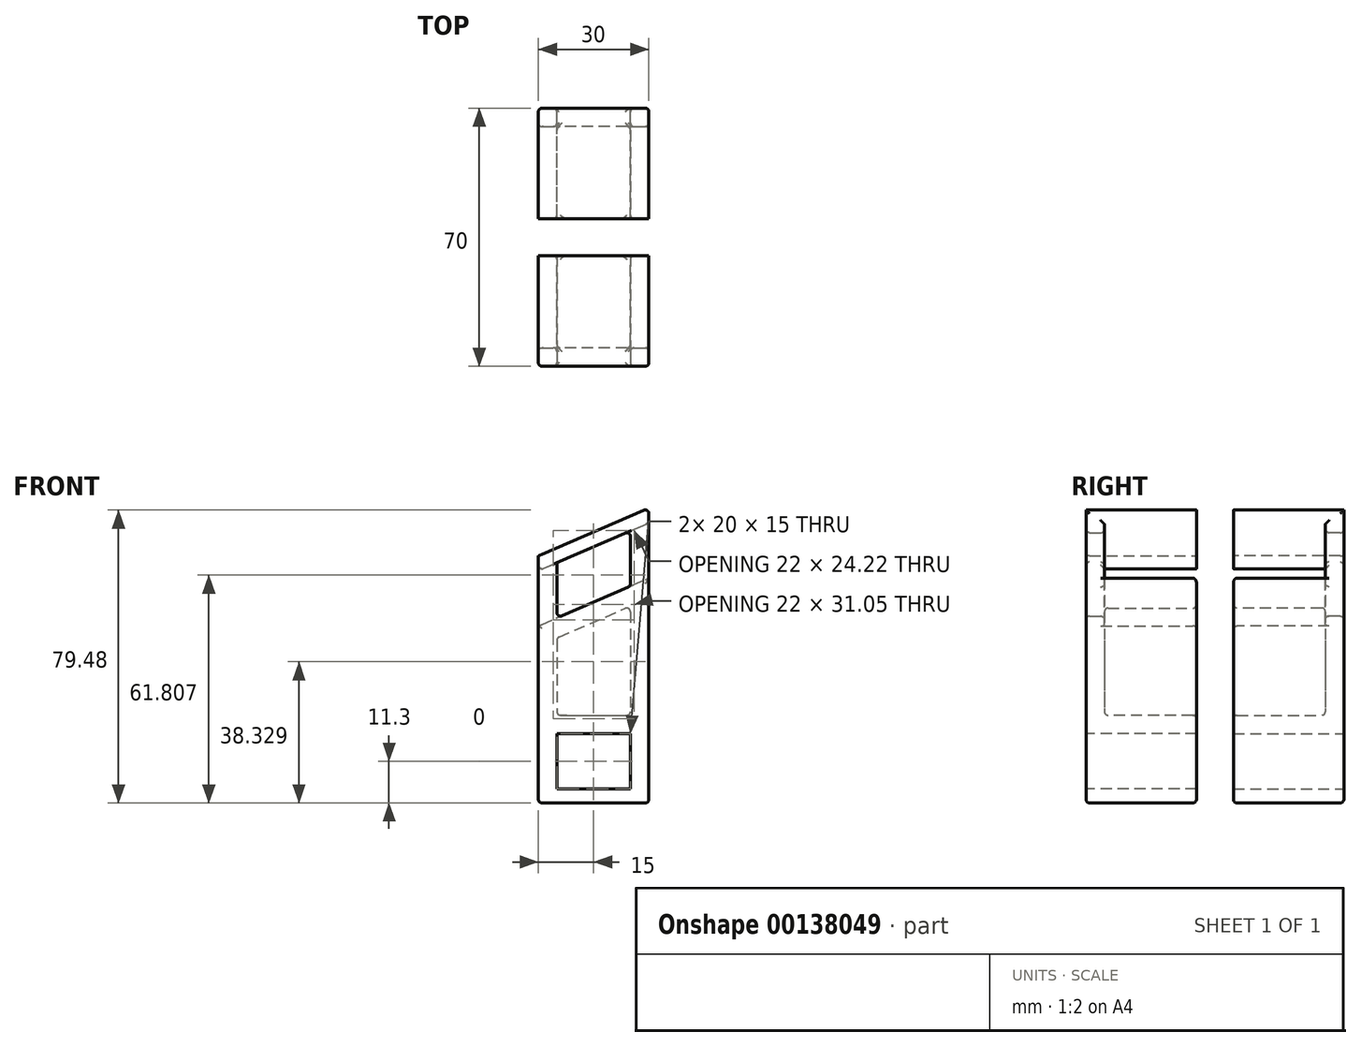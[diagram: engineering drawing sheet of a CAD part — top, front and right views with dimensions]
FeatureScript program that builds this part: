
annotation { "Feature Type Name" : "Feature", "Feature Type Description" : "" }
export const myFeature = defineFeature(function(context is Context, id is Id, definition is map)
    precondition{}
    {
        {
            var Q0;
            Q0=qCreatedBy(makeId("Top.planeOp"),FACE);
            var sketch = newSketch(context, id + "F0", { "sketchPlane" : qUnion([Q0])});
            skLineSegment(sketch, "E0.bottom", {"start": v(-15, 15) * mm, "end": v(15, 15) * mm});
            skLineSegment(sketch, "E0.top", {"start": v(-15, -15) * mm, "end": v(15, -15) * mm});
            skLineSegment(sketch, "E0.left", {"start": v(-15, 15) * mm, "end": v(-15, -15) * mm});
            skLineSegment(sketch, "E0.right", {"start": v(15, 15) * mm, "end": v(15, -15) * mm});
            skSolve(sketch);
        }
        {
            var Q0;
            Q0 = qSketchRegion(id + "F0", true);
            extrude(context, id + "F1", {"entities" : qUnion([Q0]), "depth" : 80 * mm});
        }
        {
            var Q0;
            Q0=qCreatedBy(makeId("Top.planeOp"),FACE);
            cPlane(context, id + "F2", {"entities" : qUnion([Q0]), "cplaneType" : CPlaneType.OFFSET, "offset" : 76 * mm, "width" : 152.4 * mm, "height" : 152.4 * mm});
        }
        {
            var Q0;
            Q0=qCreatedBy(id+"F2.planeOp",FACE);
            var sketch = newSketch(context, id + "F3", { "sketchPlane" : qUnion([Q0])});
            skLineSegment(sketch, "E1", {"start": v(15.02, 15.02) * mm, "end": v(15.02, -15.02) * mm});
            skSolve(sketch);
        }
        {
            var Q0;
            Q0=makeQuery(id+"F1.opExtrude","SWEPT_FACE",FACE,{"disambiguationData":[OSD([sQuery(id+"F0.wireOp",EDGE,"E0.right")])]});
            var sketch = newSketch(context, id + "F4", { "sketchPlane" : qUnion([Q0])});
            skLineSegment(sketch, "E2.bottom", {"start": v(-15, 76) * mm, "end": v(15, 76) * mm});
            skLineSegment(sketch, "E2.top", {"start": v(-15, 61) * mm, "end": v(15, 61) * mm});
            skLineSegment(sketch, "E2.left", {"start": v(-15, 76) * mm, "end": v(-15, 61) * mm});
            skLineSegment(sketch, "E2.right", {"start": v(15, 76) * mm, "end": v(15, 61) * mm});
            skSolve(sketch);
        }
        {
            var Q0;
            Q0=makeQuery(id+"F1.opExtrude","SWEPT_FACE",FACE,{"disambiguationData":[OSD([sQuery(id+"F0.wireOp",EDGE,"E0.left")])]});
            var sketch = newSketch(context, id + "F5", { "sketchPlane" : qUnion([Q0])});
            skLineSegment(sketch, "E3.bottom", {"start": v(-15, 63) * mm, "end": v(15, 63) * mm});
            skLineSegment(sketch, "E3.top", {"start": v(-15, 48) * mm, "end": v(15, 48) * mm});
            skLineSegment(sketch, "E3.left", {"start": v(-15, 63) * mm, "end": v(-15, 48) * mm});
            skLineSegment(sketch, "E3.right", {"start": v(15, 63) * mm, "end": v(15, 48) * mm});
            skSolve(sketch);
        }
        {
            var Q1;
            Q1=makeQuery(id+"F5.imprint","IMPRINT",FACE,{"disambiguationData":[TD([[makeQuery(id+"F5.imprint","IMPRINT",EDGE,{"derivedFrom":sQuery(id+"F5.wireOp",EDGE,"E3.bottom")}),-1.0]])]});
            var Q2;
            Q2=makeQuery(id+"F4.imprint","IMPRINT",FACE,{"disambiguationData":[TD([[makeQuery(id+"F4.imprint","IMPRINT",EDGE,{"derivedFrom":sQuery(id+"F4.wireOp",EDGE,"E2.bottom")}),-1.0]])]});
            loft(context, id + "F6", {"operationType" : NewBodyOperationType.REMOVE, "sheetProfilesArray" : [{ "sheetProfileEntities" : qUnion([Q1]) }, { "sheetProfileEntities" : qUnion([Q2]) }]});
        }
        {
            var Q0;
            Q0=makeQuery(id+"F1.opExtrude","CAP_FACE",FACE,{"disambiguationData":[OSD([sQuery(id+"F0.wireOp",EDGE,"E0.bottom"),sQuery(id+"F0.wireOp",EDGE,"E0.top"),sQuery(id+"F0.wireOp",EDGE,"E0.left"),sQuery(id+"F0.wireOp",EDGE,"E0.right")])],"isStart":false});
            var sketch = newSketch(context, id + "F7", { "sketchPlane" : qUnion([Q0])});
            skLineSegment(sketch, "E4.bottom", {"start": v(15, 15) * mm, "end": v(-15, 15) * mm});
            skLineSegment(sketch, "E4.top", {"start": v(15, 10) * mm, "end": v(-15, 10) * mm});
            skLineSegment(sketch, "E4.left", {"start": v(15, 15) * mm, "end": v(15, 10) * mm});
            skLineSegment(sketch, "E4.right", {"start": v(-15, 15) * mm, "end": v(-15, 10) * mm});
            skSolve(sketch);
        }
        {
            var Q0;
            Q0=makeQuery(id+"F7.imprint","IMPRINT",FACE,{"disambiguationData":[TD([[makeQuery(id+"F7.imprint","IMPRINT",EDGE,{"derivedFrom":sQuery(id+"F7.wireOp",EDGE,"E4.bottom")}),-1.0]])]});
            var Q1;
            Q1=makeQuery(id+"F6.boolean.opBoolean","SPLIT",BODY,{"disambiguationData":[OD(0.0)],"derivedFrom":makeQuery(id+"F1.opExtrude","SWEPT_BODY",BODY,{"disambiguationData":[OSD([sQuery(id+"F0.wireOp",EDGE,"E0.bottom"),sQuery(id+"F0.wireOp",EDGE,"E0.top"),sQuery(id+"F0.wireOp",EDGE,"E0.left"),sQuery(id+"F0.wireOp",EDGE,"E0.right")])]})});
            extrude(context, id + "F8", {"entities" : qUnion([Q0]), "oppositeDirection" : true, "endBoundEntityBody" : qUnion([Q1]), "depth" : 76.2 * mm});
        }
        {
            var Q0;
            Q0=makeQuery(id+"F8.opExtrude","SWEPT_FACE",FACE,{"disambiguationData":[OSD([sQuery(id+"F7.wireOp",EDGE,"E4.bottom")])]});
            var sketch = newSketch(context, id + "F9", { "sketchPlane" : qUnion([Q0])});
            skLineSegment(sketch, "E5", {"start": v(-15, 3.8) * mm, "end": v(-15, 18.8) * mm});
            skLineSegment(sketch, "E6", {"start": v(15, 3.8) * mm, "end": v(15, 18.8) * mm});
            skLineSegment(sketch, "E7", {"start": v(15, 18.8) * mm, "end": v(-15, 18.8) * mm});
            skLineSegment(sketch, "E8", {"start": v(15, 3.8) * mm, "end": v(-15, 3.8) * mm});
            skSolve(sketch);
        }
        {
            var Q0;
            Q0=makeQuery(id+"F9.imprint","IMPRINT",FACE,{"disambiguationData":[TD([[makeQuery(id+"F9.imprint","IMPRINT",EDGE,{"derivedFrom":sQuery(id+"F9.wireOp",EDGE,"E5")}),-1.0]])]});
            var sketch = newSketch(context, id + "F10", { "sketchPlane" : qUnion([Q0])});
            skLineSegment(sketch, "E9.0", {"start": v(-10, 3.8) * mm, "end": v(-10, 18.8) * mm});
            skLineSegment(sketch, "E10.0", {"start": v(10, 3.8) * mm, "end": v(10, 18.8) * mm});
            skLineSegment(sketch, "E11", {"start": v(-10, 18.8) * mm, "end": v(10, 18.8) * mm});
            skLineSegment(sketch, "E12", {"start": v(-10, 3.8) * mm, "end": v(10, 3.8) * mm});
            skSolve(sketch);
        }
        {
            var Q0;
            Q0=makeQuery(id+"F10.imprint","IMPRINT",FACE,{"disambiguationData":[TD([[makeQuery(id+"F10.imprint","IMPRINT",EDGE,{"derivedFrom":sQuery(id+"F10.wireOp",EDGE,"E9.0")}),-1.0]])]});
            extrude(context, id + "F11", {"entities" : qUnion([Q0]), "operationType" : NewBodyOperationType.REMOVE, "endBound" : BoundingType.THROUGH_ALL, "oppositeDirection" : true, "depth" : 25.4 * mm});
        }
        {
            var Q0;
            {var subQ0=sQuery(id+"F0.wireOp",EDGE,"E0.right");var subQ1=sQuery(id+"F0.wireOp",EDGE,"E0.left");var subQ2=sQuery(id+"F0.wireOp",EDGE,"E0.top");var subQ3=sQuery(id+"F0.wireOp",EDGE,"E0.bottom");Q0=makeQuery(id+"F6.boolean.opBoolean","SPLIT",FACE,{"disambiguationData":[TD([makeQuery(id+"F1.opExtrude","CAP_FACE",FACE,{"disambiguationData":[OSD([subQ3,subQ2,subQ1,subQ0])],"isStart":true})])],"derivedFrom":makeQuery(id+"F1.opExtrude","SWEPT_FACE",FACE,{"disambiguationData":[OSD([subQ2])]})});}
            shell(context, id + "F12", {"entities" : qUnion([Q0]), "thickness" : 5 * mm});
        }
        {
            var Q0;
            {var subQ0=sQuery(id+"F9.wireOp",EDGE,"E7");Q0=makeQuery(id+"F9.imprint","IMPRINT",FACE,{"disambiguationData":[TD([[makeQuery(id+"F9.imprint","IMPRINT",EDGE,{"derivedFrom":subQ0}),-1.0]])]});}
            var sketch = newSketch(context, id + "F13", { "sketchPlane" : qUnion([Q0])});
            skLineSegment(sketch, "E13", {"start": v(-10, 73.83) * mm, "end": v(10, 65.17) * mm});
            skLineSegment(sketch, "E14", {"start": v(10, 65.17) * mm, "end": v(10, 50.17) * mm});
            skLineSegment(sketch, "E15", {"start": v(10, 50.17) * mm, "end": v(-10, 58.83) * mm});
            skLineSegment(sketch, "E16", {"start": v(-10, 58.83) * mm, "end": v(-10, 73.83) * mm});
            skSolve(sketch);
        }
        {
            var Q0;
            Q0=makeQuery(id+"F13.imprint","IMPRINT",FACE,{"disambiguationData":[TD([[makeQuery(id+"F13.imprint","IMPRINT",EDGE,{"derivedFrom":sQuery(id+"F13.wireOp",EDGE,"E13")}),-1.0]])]});
            extrude(context, id + "F14", {"entities" : qUnion([Q0]), "operationType" : NewBodyOperationType.REMOVE, "oppositeDirection" : true, "depth" : 25.4 * mm});
        }
        {
            var Q0;
            Q0=makeQuery(id+"F14.boolean.opBoolean","COPY",FACE,{"derivedFrom":makeQuery(id+"F14.opExtrude","SWEPT_FACE",FACE,{"disambiguationData":[OSD([sQuery(id+"F13.wireOp",EDGE,"E16")])]})});
            var Q1;
            Q1=makeQuery(id+"F14.boolean.opBoolean","COPY",FACE,{"derivedFrom":makeQuery(id+"F14.opExtrude","SWEPT_FACE",FACE,{"disambiguationData":[OSD([sQuery(id+"F13.wireOp",EDGE,"E15")])]})});
            var Q2;
            Q2=makeQuery(id+"F14.boolean.opBoolean","COPY",FACE,{"derivedFrom":makeQuery(id+"F14.opExtrude","SWEPT_FACE",FACE,{"disambiguationData":[OSD([sQuery(id+"F13.wireOp",EDGE,"E14")])]})});
            var Q3;
            Q3=makeQuery(id+"F14.boolean.opBoolean","COPY",EDGE,{"derivedFrom":makeQuery(id+"F14.opExtrude","CAP_EDGE",EDGE,{"disambiguationData":[OSD([sQuery(id+"F13.wireOp",EDGE,"E13")])],"isStart":true})});
            fillet(context, id + "F15", {"entities" : qUnion([Q0, Q1, Q2, Q3]), "radius" : 1 * mm, "tangentPropagation" : true, "allowEdgeOverflow" : false});
        }
        {
            var Q0;
            Q0=makeQuery(id+"F12.opShell","OFFSET_FACE",FACE,{"disambiguationData":[OSD([sQuery(id+"F0.wireOp",EDGE,"E0.right")])]});
            var Q1;
            Q1=makeQuery(id+"F12.opShell","OFFSET_FACE",FACE,{"disambiguationData":[OSD([sQuery(id+"F0.wireOp",EDGE,"E0.bottom"),sQuery(id+"F0.wireOp",EDGE,"E0.top"),sQuery(id+"F0.wireOp",EDGE,"E0.left"),sQuery(id+"F0.wireOp",EDGE,"E0.right"),sQuery(id+"F4.wireOp",EDGE,"E2.top"),sQuery(id+"F4.wireOp",EDGE,"E2.left"),sQuery(id+"F4.wireOp",EDGE,"E2.right"),sQuery(id+"F5.wireOp",EDGE,"E3.top"),sQuery(id+"F5.wireOp",EDGE,"E3.left"),sQuery(id+"F5.wireOp",EDGE,"E3.right")])]});
            var Q2;
            Q2=makeQuery(id+"F12.opShell","OFFSET_FACE",FACE,{"disambiguationData":[OSD([sQuery(id+"F0.wireOp",EDGE,"E0.bottom"),sQuery(id+"F0.wireOp",EDGE,"E0.top"),sQuery(id+"F0.wireOp",EDGE,"E0.left"),sQuery(id+"F0.wireOp",EDGE,"E0.right")])]});
            var Q3;
            Q3=makeQuery(id+"F12.opShell","OFFSET_FACE",FACE,{"disambiguationData":[OSD([sQuery(id+"F0.wireOp",EDGE,"E0.left")])]});
            var Q4;
            Q4=makeQuery(id+"F12.opShell","OFFSET_FACE",FACE,{"disambiguationData":[OSD([sQuery(id+"F0.wireOp",EDGE,"E0.bottom")])]});
            fillet(context, id + "F16", {"entities" : qUnion([Q0, Q1, Q2, Q3, Q4]), "radius" : 1 * mm, "tangentPropagation" : true, "allowEdgeOverflow" : false});
        }
        {
            var Q0;
            {var subQ0=sQuery(id+"F0.wireOp",EDGE,"E0.right");var subQ1=sQuery(id+"F0.wireOp",EDGE,"E0.left");var subQ2=sQuery(id+"F0.wireOp",EDGE,"E0.top");var subQ3=sQuery(id+"F0.wireOp",EDGE,"E0.bottom");Q0=makeQuery(id+"F6.boolean.opBoolean","SPLIT",FACE,{"disambiguationData":[TD([makeQuery(id+"F1.opExtrude","CAP_FACE",FACE,{"disambiguationData":[OSD([subQ3,subQ2,subQ1,subQ0])],"isStart":false})])],"derivedFrom":makeQuery(id+"F1.opExtrude","SWEPT_FACE",FACE,{"disambiguationData":[OSD([subQ2])]})});}
            var sketch = newSketch(context, id + "F17", { "sketchPlane" : qUnion([Q0])});
            skLineSegment(sketch, "E17", {"start": v(-15, 67) * mm, "end": v(15, 80) * mm});
            skLineSegment(sketch, "E18", {"start": v(-15, 67) * mm, "end": v(-15, 80) * mm});
            skLineSegment(sketch, "E19", {"start": v(-15, 80) * mm, "end": v(15, 80) * mm});
            skSolve(sketch);
        }
        {
            var Q0;
            Q0=makeQuery(id+"F17.imprint","IMPRINT",FACE,{"disambiguationData":[TD([[makeQuery(id+"F17.imprint","IMPRINT",EDGE,{"derivedFrom":sQuery(id+"F17.wireOp",EDGE,"E17")}),1.0]])]});
            var Q1;
            Q1=makeQuery(id+"F8.opExtrude","SWEPT_FACE",FACE,{"disambiguationData":[OSD([sQuery(id+"F7.wireOp",EDGE,"E4.bottom")])]});
            extrude(context, id + "F18", {"entities" : qUnion([Q0]), "operationType" : NewBodyOperationType.REMOVE, "endBound" : BoundingType.UP_TO_SURFACE, "oppositeDirection" : true, "endBoundEntityFace" : qUnion([Q1]), "depth" : 25.4 * mm});
        }
        {
            var Q0;
            {var subQ0=sQuery(id+"F9.wireOp",EDGE,"E7");Q0=makeQuery(id+"F9.imprint","IMPRINT",FACE,{"disambiguationData":[TD([[makeQuery(id+"F9.imprint","IMPRINT",EDGE,{"derivedFrom":subQ0}),-1.0]])]});}
            var sketch = newSketch(context, id + "F19", { "sketchPlane" : qUnion([Q0])});
            skLineSegment(sketch, "E20", {"start": v(-15, 80) * mm, "end": v(15, 67) * mm});
            skLineSegment(sketch, "E21", {"start": v(-15, 80) * mm, "end": v(15, 80) * mm});
            skLineSegment(sketch, "E22", {"start": v(15, 80) * mm, "end": v(15, 67) * mm});
            skSolve(sketch);
        }
        {
            var Q0;
            Q0=makeQuery(id+"F19.imprint","IMPRINT",FACE,{"disambiguationData":[TD([[makeQuery(id+"F19.imprint","IMPRINT",EDGE,{"derivedFrom":sQuery(id+"F19.wireOp",EDGE,"E20")}),1.0]])]});
            extrude(context, id + "F20", {"entities" : qUnion([Q0]), "operationType" : NewBodyOperationType.REMOVE, "endBound" : BoundingType.THROUGH_ALL, "oppositeDirection" : true, "depth" : 25.4 * mm});
        }
        {
            var Q0;
            Q0=makeQuery(id+"F8.opExtrude","SWEPT_BODY",BODY,{"disambiguationData":[OSD([sQuery(id+"F7.wireOp",EDGE,"E4.bottom"),sQuery(id+"F7.wireOp",EDGE,"E4.top"),sQuery(id+"F7.wireOp",EDGE,"E4.left"),sQuery(id+"F7.wireOp",EDGE,"E4.right")])]});
            var Q1;
            Q1=makeQuery(id+"F6.boolean.opBoolean","SPLIT",BODY,{"disambiguationData":[OD(1.0)],"derivedFrom":makeQuery(id+"F1.opExtrude","SWEPT_BODY",BODY,{"disambiguationData":[OSD([sQuery(id+"F0.wireOp",EDGE,"E0.bottom"),sQuery(id+"F0.wireOp",EDGE,"E0.top"),sQuery(id+"F0.wireOp",EDGE,"E0.left"),sQuery(id+"F0.wireOp",EDGE,"E0.right")])]})});
            var Q2;
            Q2=makeQuery(id+"F6.boolean.opBoolean","SPLIT",BODY,{"disambiguationData":[OD(0.0)],"derivedFrom":makeQuery(id+"F1.opExtrude","SWEPT_BODY",BODY,{"disambiguationData":[OSD([sQuery(id+"F0.wireOp",EDGE,"E0.bottom"),sQuery(id+"F0.wireOp",EDGE,"E0.top"),sQuery(id+"F0.wireOp",EDGE,"E0.left"),sQuery(id+"F0.wireOp",EDGE,"E0.right")])]})});
            booleanBodies(context, id + "F21", {"operationType" : BooleanOperationType.UNION, "tools" : qUnion([Q0, Q1, Q2])});
        }
        {
            var Q0;
            {var subQ0=sQuery(id+"F0.wireOp",EDGE,"E0.right");var subQ1=sQuery(id+"F0.wireOp",EDGE,"E0.left");var subQ2=sQuery(id+"F0.wireOp",EDGE,"E0.top");var subQ3=sQuery(id+"F0.wireOp",EDGE,"E0.bottom");Q0=makeQuery(id+"F6.boolean.opBoolean","SPLIT",EDGE,{"disambiguationData":[TD([makeQuery(id+"F1.opExtrude","CAP_FACE",FACE,{"disambiguationData":[OSD([subQ3,subQ2,subQ1,subQ0])],"isStart":true})])],"derivedFrom":makeQuery(id+"F1.opExtrude","SWEPT_EDGE",EDGE,{"disambiguationData":[OSD([subQ2,subQ0])]})});}
            var Q1;
            Q1=makeQuery(id+"F6.boolean.opBoolean","COPY",EDGE,{"derivedFrom":makeQuery(id+"F6.opLoft","MID_CAP_EDGE",EDGE,{"disambiguationData":[OSD([sQuery(id+"F0.wireOp",EDGE,"E0.bottom"),sQuery(id+"F0.wireOp",EDGE,"E0.top"),sQuery(id+"F0.wireOp",EDGE,"E0.right"),sQuery(id+"F4.wireOp",EDGE,"E2.top"),sQuery(id+"F4.wireOp",EDGE,"E2.left"),sQuery(id+"F4.wireOp",EDGE,"E2.right")])],"capPos":1.0})});
            var Q2;
            Q2=makeQuery(id+"F6.boolean.opBoolean","COPY",EDGE,{"derivedFrom":makeQuery(id+"F6.opLoft","SWEPT_EDGE",EDGE,{"disambiguationData":[OSD([sQuery(id+"F0.wireOp",EDGE,"E0.top"),sQuery(id+"F0.wireOp",EDGE,"E0.left"),sQuery(id+"F0.wireOp",EDGE,"E0.right"),sQuery(id+"F4.wireOp",EDGE,"E2.top"),sQuery(id+"F4.wireOp",EDGE,"E2.left"),sQuery(id+"F5.wireOp",EDGE,"E3.top"),sQuery(id+"F5.wireOp",EDGE,"E3.right")])]})});
            var Q3;
            {var subQ0=sQuery(id+"F0.wireOp",EDGE,"E0.right");var subQ1=sQuery(id+"F0.wireOp",EDGE,"E0.left");var subQ2=sQuery(id+"F0.wireOp",EDGE,"E0.top");var subQ3=sQuery(id+"F0.wireOp",EDGE,"E0.bottom");Q3=makeQuery(id+"F6.boolean.opBoolean","SPLIT",EDGE,{"disambiguationData":[TD([makeQuery(id+"F1.opExtrude","CAP_FACE",FACE,{"disambiguationData":[OSD([subQ3,subQ2,subQ1,subQ0])],"isStart":true})])],"derivedFrom":makeQuery(id+"F1.opExtrude","SWEPT_EDGE",EDGE,{"disambiguationData":[OSD([subQ2,subQ1])]})});}
            var Q4;
            Q4=makeQuery(id+"F1.opExtrude","CAP_EDGE",EDGE,{"disambiguationData":[OSD([sQuery(id+"F0.wireOp",EDGE,"E0.top")])],"isStart":true});
            var Q5;
            Q5=makeQuery(id+"F1.opExtrude","CAP_EDGE",EDGE,{"disambiguationData":[OSD([sQuery(id+"F0.wireOp",EDGE,"E0.right")])],"isStart":true});
            var Q6;
            {var subQ0=sQuery(id+"F0.wireOp",EDGE,"E0.bottom");var subQ1=sQuery(id+"F0.wireOp",EDGE,"E0.right");var subQ2=sQuery(id+"F0.wireOp",EDGE,"E0.left");var subQ3=sQuery(id+"F0.wireOp",EDGE,"E0.top");Q6=makeQuery(id+"F21.opBoolean","MERGE",EDGE,{"derivedFrom":[makeQuery(id+"F6.boolean.opBoolean","SPLIT",EDGE,{"disambiguationData":[TD([makeQuery(id+"F1.opExtrude","CAP_FACE",FACE,{"disambiguationData":[OSD([subQ0,subQ3,subQ2,subQ1])],"isStart":true})])],"derivedFrom":makeQuery(id+"F1.opExtrude","SWEPT_EDGE",EDGE,{"disambiguationData":[OSD([subQ0,subQ1])]})}),makeQuery(id+"F8.opExtrude","SWEPT_EDGE",EDGE,{"disambiguationData":[OSD([sQuery(id+"F7.wireOp",EDGE,"E4.bottom"),sQuery(id+"F7.wireOp",EDGE,"E4.left")])]})]});}
            var Q7;
            {var subQ0=sQuery(id+"F7.wireOp",EDGE,"E4.left");var subQ1=sQuery(id+"F0.wireOp",EDGE,"E0.right");Q7=makeQuery(id+"F21.opBoolean","MERGE",EDGE,{"derivedFrom":[makeQuery(id+"F18.boolean.opBoolean","MERGE",EDGE,{"derivedFrom":[makeQuery(id+"F1.opExtrude","CAP_EDGE",EDGE,{"disambiguationData":[OSD([subQ1])],"isStart":false}),makeQuery(id+"F18.opExtrude","SWEPT_EDGE",EDGE,{"disambiguationData":[OSD([sQuery(id+"F0.wireOp",EDGE,"E0.top"),subQ1,sQuery(id+"F17.wireOp",EDGE,"E17"),sQuery(id+"F17.wireOp",EDGE,"E19")])]})]}),makeQuery(id+"F20.boolean.opBoolean","MERGE",EDGE,{"derivedFrom":[makeQuery(id+"F8.opExtrude","CAP_EDGE",EDGE,{"disambiguationData":[OSD([subQ0])],"isStart":true}),makeQuery(id+"F20.opExtrude","SWEPT_EDGE",EDGE,{"disambiguationData":[OSD([sQuery(id+"F7.wireOp",EDGE,"E4.bottom"),subQ0,sQuery(id+"F19.wireOp",EDGE,"E20"),sQuery(id+"F19.wireOp",EDGE,"E21")])]})]})]});}
            var Q8;
            Q8=makeQuery(id+"F18.boolean.opBoolean","COPY",EDGE,{"derivedFrom":makeQuery(id+"F18.opExtrude","CAP_EDGE",EDGE,{"disambiguationData":[OSD([sQuery(id+"F17.wireOp",EDGE,"E17")])],"isStart":true})});
            var Q9;
            Q9=makeQuery(id+"F21.opBoolean","MERGE",EDGE,{"derivedFrom":[makeQuery(id+"F18.boolean.opBoolean","COPY",EDGE,{"derivedFrom":makeQuery(id+"F18.opExtrude","SWEPT_EDGE",EDGE,{"disambiguationData":[OSD([sQuery(id+"F0.wireOp",EDGE,"E0.top"),sQuery(id+"F0.wireOp",EDGE,"E0.left"),sQuery(id+"F17.wireOp",EDGE,"E17"),sQuery(id+"F17.wireOp",EDGE,"E18")])]})}),makeQuery(id+"F20.boolean.opBoolean","COPY",EDGE,{"derivedFrom":makeQuery(id+"F20.opExtrude","SWEPT_EDGE",EDGE,{"disambiguationData":[OSD([sQuery(id+"F7.wireOp",EDGE,"E4.bottom"),sQuery(id+"F7.wireOp",EDGE,"E4.right"),sQuery(id+"F19.wireOp",EDGE,"E20"),sQuery(id+"F19.wireOp",EDGE,"E22")])]})})]});
            var Q10;
            Q10=makeQuery(id+"F20.boolean.opBoolean","COPY",EDGE,{"derivedFrom":makeQuery(id+"F20.opExtrude","CAP_EDGE",EDGE,{"disambiguationData":[OSD([sQuery(id+"F19.wireOp",EDGE,"E20")])],"isStart":true})});
            var Q11;
            Q11=makeQuery(id+"F8.opExtrude","SWEPT_EDGE",EDGE,{"disambiguationData":[OSD([sQuery(id+"F0.wireOp",EDGE,"E0.right"),sQuery(id+"F7.wireOp",EDGE,"E4.top"),sQuery(id+"F7.wireOp",EDGE,"E4.left")])]});
            var Q12;
            Q12=makeQuery(id+"F6.boolean.opBoolean","COPY",EDGE,{"derivedFrom":makeQuery(id+"F6.opLoft","MID_CAP_EDGE",EDGE,{"disambiguationData":[OSD([sQuery(id+"F0.wireOp",EDGE,"E0.bottom"),sQuery(id+"F0.wireOp",EDGE,"E0.top"),sQuery(id+"F0.wireOp",EDGE,"E0.right"),sQuery(id+"F4.wireOp",EDGE,"E2.bottom"),sQuery(id+"F4.wireOp",EDGE,"E2.left"),sQuery(id+"F4.wireOp",EDGE,"E2.right")])],"capPos":1.0})});
            var Q13;
            Q13=makeQuery(id+"F6.boolean.opBoolean","COPY",EDGE,{"derivedFrom":makeQuery(id+"F6.opLoft","SWEPT_EDGE",EDGE,{"disambiguationData":[OSD([sQuery(id+"F0.wireOp",EDGE,"E0.top"),sQuery(id+"F0.wireOp",EDGE,"E0.left"),sQuery(id+"F0.wireOp",EDGE,"E0.right"),sQuery(id+"F4.wireOp",EDGE,"E2.bottom"),sQuery(id+"F4.wireOp",EDGE,"E2.left"),sQuery(id+"F5.wireOp",EDGE,"E3.bottom"),sQuery(id+"F5.wireOp",EDGE,"E3.right")])]})});
            var Q14;
            Q14=makeQuery(id+"F1.opExtrude","CAP_EDGE",EDGE,{"disambiguationData":[OSD([sQuery(id+"F0.wireOp",EDGE,"E0.left")])],"isStart":true});
            var Q15;
            Q15=makeQuery(id+"F1.opExtrude","CAP_EDGE",EDGE,{"disambiguationData":[OSD([sQuery(id+"F0.wireOp",EDGE,"E0.bottom")])],"isStart":true});
            var Q16;
            {var subQ0=sQuery(id+"F0.wireOp",EDGE,"E0.bottom");var subQ1=sQuery(id+"F0.wireOp",EDGE,"E0.right");var subQ2=sQuery(id+"F0.wireOp",EDGE,"E0.left");var subQ3=sQuery(id+"F0.wireOp",EDGE,"E0.top");Q16=makeQuery(id+"F21.opBoolean","MERGE",EDGE,{"derivedFrom":[makeQuery(id+"F6.boolean.opBoolean","SPLIT",EDGE,{"disambiguationData":[TD([makeQuery(id+"F1.opExtrude","CAP_FACE",FACE,{"disambiguationData":[OSD([subQ0,subQ3,subQ2,subQ1])],"isStart":true})])],"derivedFrom":makeQuery(id+"F1.opExtrude","SWEPT_EDGE",EDGE,{"disambiguationData":[OSD([subQ0,subQ2])]})}),makeQuery(id+"F8.opExtrude","SWEPT_EDGE",EDGE,{"disambiguationData":[OSD([sQuery(id+"F7.wireOp",EDGE,"E4.bottom"),sQuery(id+"F7.wireOp",EDGE,"E4.right")])]})]});}
            var Q17;
            Q17=makeQuery(id+"F6.boolean.opBoolean","COPY",EDGE,{"derivedFrom":makeQuery(id+"F6.opLoft","MID_CAP_EDGE",EDGE,{"disambiguationData":[OSD([sQuery(id+"F0.wireOp",EDGE,"E0.bottom"),sQuery(id+"F0.wireOp",EDGE,"E0.top"),sQuery(id+"F0.wireOp",EDGE,"E0.left"),sQuery(id+"F5.wireOp",EDGE,"E3.bottom"),sQuery(id+"F5.wireOp",EDGE,"E3.left"),sQuery(id+"F5.wireOp",EDGE,"E3.right")])],"capPos":0.0})});
            var Q18;
            Q18=makeQuery(id+"F8.opExtrude","SWEPT_EDGE",EDGE,{"disambiguationData":[OSD([sQuery(id+"F0.wireOp",EDGE,"E0.left"),sQuery(id+"F7.wireOp",EDGE,"E4.top"),sQuery(id+"F7.wireOp",EDGE,"E4.right")])]});
            var Q19;
            Q19=makeQuery(id+"F6.boolean.opBoolean","COPY",EDGE,{"derivedFrom":makeQuery(id+"F6.opLoft","MID_CAP_EDGE",EDGE,{"disambiguationData":[OSD([sQuery(id+"F0.wireOp",EDGE,"E0.bottom"),sQuery(id+"F0.wireOp",EDGE,"E0.top"),sQuery(id+"F0.wireOp",EDGE,"E0.left"),sQuery(id+"F5.wireOp",EDGE,"E3.top"),sQuery(id+"F5.wireOp",EDGE,"E3.left"),sQuery(id+"F5.wireOp",EDGE,"E3.right")])],"capPos":0.0})});
            fillet(context, id + "F22", {"entities" : qUnion([Q0, Q1, Q2, Q3, Q4, Q5, Q6, Q7, Q8, Q9, Q10, Q11, Q12, Q13, Q14, Q15, Q16, Q17, Q18, Q19]), "radius" : 1 * mm, "tangentPropagation" : true, "allowEdgeOverflow" : false});
        }
        {
            var Q0;
            Q0=makeQuery(id+"F6.boolean.opBoolean","COPY",EDGE,{"derivedFrom":makeQuery(id+"F6.opLoft","SWEPT_EDGE",EDGE,{"disambiguationData":[OSD([sQuery(id+"F0.wireOp",EDGE,"E0.bottom"),sQuery(id+"F0.wireOp",EDGE,"E0.left"),sQuery(id+"F0.wireOp",EDGE,"E0.right"),sQuery(id+"F4.wireOp",EDGE,"E2.top"),sQuery(id+"F4.wireOp",EDGE,"E2.right"),sQuery(id+"F5.wireOp",EDGE,"E3.top"),sQuery(id+"F5.wireOp",EDGE,"E3.left")])]})});
            fillet(context, id + "F23", {"entities" : qUnion([Q0]), "radius" : 1 * mm, "tangentPropagation" : true, "allowEdgeOverflow" : false});
        }
        {
            var Q0;
            Q0=qCreatedBy(makeId("Front.planeOp"),FACE);
            cPlane(context, id + "F24", {"entities" : qUnion([Q0]), "cplaneType" : CPlaneType.OFFSET, "offset" : 20 * mm, "width" : 152.4 * mm, "height" : 152.4 * mm});
        }
        {
            var Q0;
            Q0=makeQuery(id+"F8.opExtrude","SWEPT_BODY",BODY,{"disambiguationData":[OSD([sQuery(id+"F7.wireOp",EDGE,"E4.bottom"),sQuery(id+"F7.wireOp",EDGE,"E4.top"),sQuery(id+"F7.wireOp",EDGE,"E4.left"),sQuery(id+"F7.wireOp",EDGE,"E4.right")])]});
            var Q1;
            Q1=qCreatedBy(id+"F24.planeOp",FACE);
            mirror(context, id + "F25", {"entities" : qUnion([Q0]), "mirrorPlane" : qUnion([Q1])});
        }
    });
